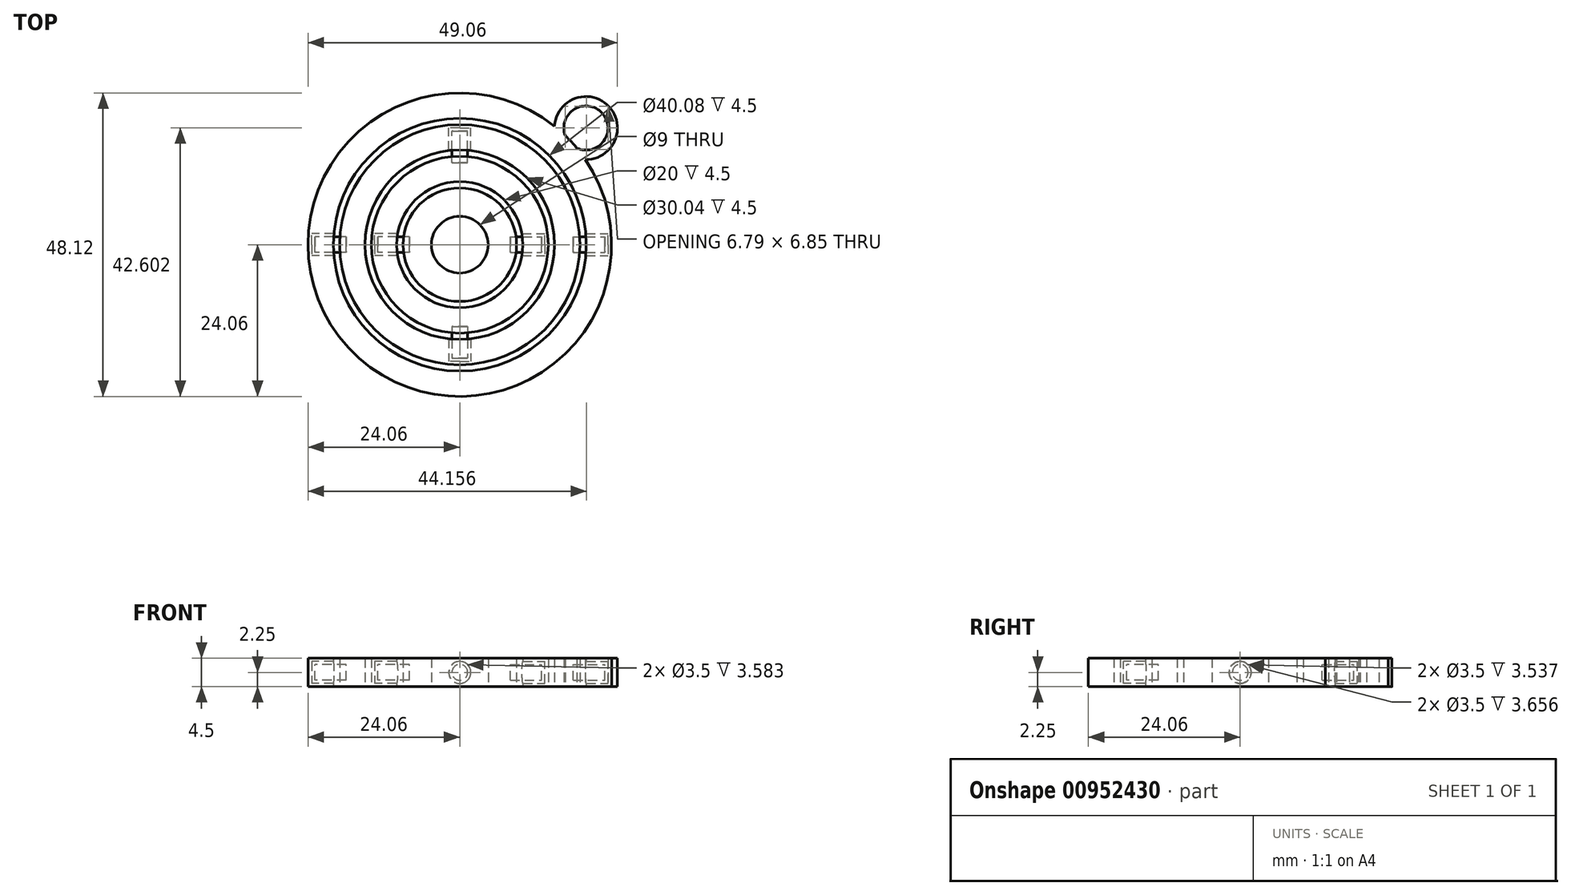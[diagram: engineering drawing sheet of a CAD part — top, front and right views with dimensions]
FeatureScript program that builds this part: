
annotation { "Feature Type Name" : "Feature", "Feature Type Description" : "" }
export const myFeature = defineFeature(function(context is Context, id is Id, definition is map)
    precondition{}
    {
        {
            var Q0;
            Q0=qCreatedBy(makeId("Top.planeOp"),FACE);
            var sketch = newSketch(context, id + "F0", { "sketchPlane" : qUnion([Q0])});
            skCircle(sketch, "E0", {"center": v(0, 0) * mm, "radius": 4.5 * mm});
            skCircle(sketch, "E1.0", {"center": v(0, 0) * mm, "radius": 9 * mm});
            skCircle(sketch, "E2.0", {"center": v(0, 0) * mm, "radius": 10 * mm});
            skCircle(sketch, "E3.0", {"center": v(0, 0) * mm, "radius": 14.02 * mm});
            skCircle(sketch, "E4.0", {"center": v(0, 0) * mm, "radius": 15.02 * mm});
            skCircle(sketch, "E5.0", {"center": v(0, 0) * mm, "radius": 19.04 * mm});
            skCircle(sketch, "E6.0", {"center": v(0, 0) * mm, "radius": 20.04 * mm});
            skCircle(sketch, "E7.0", {"center": v(0, 0) * mm, "radius": 24.06 * mm});
            skSolve(sketch);
        }
        {
            var Q0;
            Q0=qCreatedBy(makeId("Right.planeOp"),FACE);
            cPlane(context, id + "F1", {"entities" : qUnion([Q0]), "cplaneType" : CPlaneType.OFFSET, "offset" : 13 * mm, "oppositeDirection" : true, "width" : 150 * mm, "height" : 150 * mm});
        }
        {
            var Q0;
            Q0=qCreatedBy(makeId("Right.planeOp"),FACE);
            cPlane(context, id + "F2", {"entities" : qUnion([Q0]), "cplaneType" : CPlaneType.OFFSET, "offset" : 23 * mm, "oppositeDirection" : true, "width" : 150 * mm, "height" : 150 * mm});
        }
        {
            var Q0;
            Q0=makeQuery(id+"F0.imprint","IMPRINT",FACE,{"disambiguationData":[TD([[makeQuery(id+"F0.imprint","IMPRINT",EDGE,{"derivedFrom":sQuery(id+"F0.wireOp",EDGE,"E6.0")}),-1.0]])]});
            var Q1;
            Q1=makeQuery(id+"F0.imprint","IMPRINT",FACE,{"disambiguationData":[TD([[makeQuery(id+"F0.imprint","IMPRINT",EDGE,{"derivedFrom":sQuery(id+"F0.wireOp",EDGE,"E4.0")}),-1.0]])]});
            var Q2;
            Q2=makeQuery(id+"F0.imprint","IMPRINT",FACE,{"disambiguationData":[TD([[makeQuery(id+"F0.imprint","IMPRINT",EDGE,{"derivedFrom":sQuery(id+"F0.wireOp",EDGE,"E2.0")}),-1.0]])]});
            var Q3;
            Q3=makeQuery(id+"F0.imprint","IMPRINT",FACE,{"disambiguationData":[TD([[makeQuery(id+"F0.imprint","IMPRINT",EDGE,{"derivedFrom":sQuery(id+"F0.wireOp",EDGE,"E0")}),-1.0]])]});
            extrude(context, id + "F3", {"entities" : qUnion([Q0, Q1, Q2, Q3]), "depth" : 4.5 * mm, "offsetDistance" : 25 * mm});
        }
        {
            var Q0;
            Q0=qCreatedBy(id+"F1.planeOp",FACE);
            var sketch = newSketch(context, id + "F4", { "sketchPlane" : qUnion([Q0])});
            skCircle(sketch, "E8", {"center": v(0, 2.25) * mm, "radius": 1.25 * mm});
            skSolve(sketch);
        }
        {
            var Q0;
            Q0=makeQuery(id+"F4.imprint","IMPRINT",FACE,{"disambiguationData":[TD([[makeQuery(id+"F4.imprint","IMPRINT",EDGE,{"derivedFrom":sQuery(id+"F4.wireOp",EDGE,"E8")}),1.0]])]});
            extrude(context, id + "F5", {"entities" : qUnion([Q0]), "depth" : 5 * mm, "offsetDistance" : 25 * mm});
        }
        {
            var Q0;
            Q0=qCreatedBy(id+"F2.planeOp",FACE);
            var sketch = newSketch(context, id + "F6", { "sketchPlane" : qUnion([Q0])});
            skCircle(sketch, "E9.0", {"center": v(0, 2.25) * mm, "radius": 1.25 * mm});
            skSolve(sketch);
        }
        {
            var Q0;
            Q0=makeQuery(id+"F6.imprint","IMPRINT",FACE,{"disambiguationData":[TD([[makeQuery(id+"F6.imprint","IMPRINT",EDGE,{"derivedFrom":sQuery(id+"F6.wireOp",EDGE,"E9.0")}),1.0]])]});
            extrude(context, id + "F7", {"entities" : qUnion([Q0]), "depth" : 5 * mm, "offsetDistance" : 25 * mm});
        }
        {
            var Q0;
            Q0=qCreatedBy(id+"F1.planeOp",FACE);
            cPlane(context, id + "F8", {"entities" : qUnion([Q0]), "cplaneType" : CPlaneType.OFFSET, "offset" : 0.5 * mm, "oppositeDirection" : true, "width" : 150 * mm, "height" : 150 * mm});
        }
        {
            var Q0;
            Q0=qCreatedBy(id+"F2.planeOp",FACE);
            cPlane(context, id + "F9", {"entities" : qUnion([Q0]), "cplaneType" : CPlaneType.OFFSET, "offset" : 0.5 * mm, "oppositeDirection" : true, "width" : 150 * mm, "height" : 150 * mm});
        }
        {
            var Q0;
            Q0=qCreatedBy(id+"F8.planeOp",FACE);
            var sketch = newSketch(context, id + "F10", { "sketchPlane" : qUnion([Q0])});
            skCircle(sketch, "E10.0", {"center": v(0, 2.25) * mm, "radius": 1.25 * mm});
            skCircle(sketch, "E11.0", {"center": v(0, 2.25) * mm, "radius": 1.75 * mm});
            skSolve(sketch);
        }
        {
            var Q0;
            Q0=qCreatedBy(id+"F9.planeOp",FACE);
            var sketch = newSketch(context, id + "F11", { "sketchPlane" : qUnion([Q0])});
            skCircle(sketch, "E12.0", {"center": v(0, 2.25) * mm, "radius": 1.25 * mm});
            skCircle(sketch, "E13.0", {"center": v(0, 2.25) * mm, "radius": 1.75 * mm});
            skSolve(sketch);
        }
        {
            var Q0;
            Q0=makeQuery(id+"F10.imprint","IMPRINT",FACE,{"disambiguationData":[TD([[makeQuery(id+"F10.imprint","IMPRINT",EDGE,{"derivedFrom":sQuery(id+"F10.wireOp",EDGE,"E10.0")}),-1.0]])]});
            var Q1;
            Q1=makeQuery(id+"F10.imprint","IMPRINT",FACE,{"disambiguationData":[TD([[makeQuery(id+"F10.imprint","IMPRINT",EDGE,{"derivedFrom":sQuery(id+"F10.wireOp",EDGE,"E10.0")}),1.0]])]});
            extrude(context, id + "F12", {"entities" : qUnion([Q0, Q1]), "depth" : 5 * mm, "offsetDistance" : 25 * mm});
        }
        {
            var Q0;
            Q0=makeQuery(id+"F11.imprint","IMPRINT",FACE,{"disambiguationData":[TD([[makeQuery(id+"F11.imprint","IMPRINT",EDGE,{"derivedFrom":sQuery(id+"F11.wireOp",EDGE,"E12.0")}),1.0]])]});
            var Q1;
            Q1=makeQuery(id+"F11.imprint","IMPRINT",FACE,{"disambiguationData":[TD([[makeQuery(id+"F11.imprint","IMPRINT",EDGE,{"derivedFrom":sQuery(id+"F11.wireOp",EDGE,"E12.0")}),-1.0]])]});
            extrude(context, id + "F13", {"entities" : qUnion([Q0, Q1]), "depth" : 5 * mm, "offsetDistance" : 25 * mm});
        }
        {
            var Q0;
            Q0=makeQuery(id+"F5.opExtrude","SWEPT_BODY",BODY,{"disambiguationData":[OSD([sQuery(id+"F4.wireOp",EDGE,"E8")])]});
            var Q1;
            Q1=makeQuery(id+"F7.opExtrude","SWEPT_BODY",BODY,{"disambiguationData":[OSD([sQuery(id+"F6.wireOp",EDGE,"E9.0")])]});
            var Q2;
            Q2=makeQuery(id+"F12.opExtrude","SWEPT_BODY",BODY,{"disambiguationData":[OSD([sQuery(id+"F10.wireOp",EDGE,"E11.0")])]});
            var Q3;
            Q3=makeQuery(id+"F13.opExtrude","SWEPT_BODY",BODY,{"disambiguationData":[OSD([sQuery(id+"F11.wireOp",EDGE,"E13.0")])]});
            var Q4;
            Q4=qCreatedBy(makeId("Right.planeOp"),FACE);
            mirror(context, id + "F14", {"entities" : qUnion([Q0, Q1, Q2, Q3]), "mirrorPlane" : qUnion([Q4])});
        }
        {
            var Q0;
            Q0=qCreatedBy(makeId("Front.planeOp"),FACE);
            cPlane(context, id + "F15", {"entities" : qUnion([Q0]), "cplaneType" : CPlaneType.OFFSET, "offset" : 18 * mm, "oppositeDirection" : true, "width" : 150 * mm, "height" : 150 * mm});
        }
        {
            var Q0;
            Q0=qCreatedBy(id+"F15.planeOp",FACE);
            var sketch = newSketch(context, id + "F16", { "sketchPlane" : qUnion([Q0])});
            skCircle(sketch, "E14", {"center": v(0, 2.25) * mm, "radius": 1.25 * mm});
            skSolve(sketch);
        }
        {
            var Q0;
            Q0=makeQuery(id+"F16.imprint","IMPRINT",FACE,{"disambiguationData":[TD([[makeQuery(id+"F16.imprint","IMPRINT",EDGE,{"derivedFrom":sQuery(id+"F16.wireOp",EDGE,"E14")}),1.0]])]});
            extrude(context, id + "F17", {"entities" : qUnion([Q0]), "depth" : 5 * mm, "offsetDistance" : 25 * mm});
        }
        {
            var Q0;
            Q0=qCreatedBy(id+"F15.planeOp",FACE);
            cPlane(context, id + "F18", {"entities" : qUnion([Q0]), "cplaneType" : CPlaneType.OFFSET, "offset" : 0.5 * mm, "oppositeDirection" : true, "width" : 150 * mm, "height" : 150 * mm});
        }
        {
            var Q0;
            Q0=qCreatedBy(id+"F18.planeOp",FACE);
            var sketch = newSketch(context, id + "F19", { "sketchPlane" : qUnion([Q0])});
            skCircle(sketch, "E15.0", {"center": v(0, 2.25) * mm, "radius": 1.25 * mm});
            skCircle(sketch, "E16.0", {"center": v(0, 2.25) * mm, "radius": 1.75 * mm});
            skSolve(sketch);
        }
        {
            var Q0;
            Q0=makeQuery(id+"F19.imprint","IMPRINT",FACE,{"disambiguationData":[TD([[makeQuery(id+"F19.imprint","IMPRINT",EDGE,{"derivedFrom":sQuery(id+"F19.wireOp",EDGE,"E15.0")}),1.0]])]});
            var Q1;
            Q1=makeQuery(id+"F19.imprint","IMPRINT",FACE,{"disambiguationData":[TD([[makeQuery(id+"F19.imprint","IMPRINT",EDGE,{"derivedFrom":sQuery(id+"F19.wireOp",EDGE,"E15.0")}),-1.0]])]});
            extrude(context, id + "F20", {"entities" : qUnion([Q0, Q1]), "depth" : 5 * mm, "offsetDistance" : 25 * mm});
        }
        {
            var Q0;
            Q0=makeQuery(id+"F17.opExtrude","SWEPT_BODY",BODY,{"disambiguationData":[OSD([sQuery(id+"F16.wireOp",EDGE,"E14")])]});
            var Q1;
            Q1=makeQuery(id+"F20.opExtrude","SWEPT_BODY",BODY,{"disambiguationData":[OSD([sQuery(id+"F19.wireOp",EDGE,"E16.0")])]});
            var Q2;
            Q2=qCreatedBy(makeId("Front.planeOp"),FACE);
            mirror(context, id + "F21", {"entities" : qUnion([Q0, Q1]), "mirrorPlane" : qUnion([Q2])});
        }
        {
            var Q0;
            Q0=makeQuery(id+"F13.opExtrude","SWEPT_BODY",BODY,{"disambiguationData":[OSD([sQuery(id+"F11.wireOp",EDGE,"E13.0")])]});
            var Q1;
            Q1=makeQuery(id+"F14.opPattern","COPY",BODY,{"derivedFrom":makeQuery(id+"F13.opExtrude","SWEPT_BODY",BODY,{"disambiguationData":[OSD([sQuery(id+"F11.wireOp",EDGE,"E13.0")])]}),"instanceName":"1"});
            var Q2;
            Q2=makeQuery(id+"F3.opExtrude","SWEPT_BODY",BODY,{"disambiguationData":[OSD([sQuery(id+"F0.wireOp",EDGE,"E6.0"),sQuery(id+"F0.wireOp",EDGE,"E7.0")])]});
            booleanBodies(context, id + "F22", {"operationType" : BooleanOperationType.SUBTRACTION, "tools" : qUnion([Q0, Q1]), "targets" : qUnion([Q2])});
        }
        {
            var Q0;
            Q0=makeQuery(id+"F12.opExtrude","SWEPT_BODY",BODY,{"disambiguationData":[OSD([sQuery(id+"F10.wireOp",EDGE,"E11.0")])]});
            var Q1;
            Q1=makeQuery(id+"F14.opPattern","COPY",BODY,{"derivedFrom":makeQuery(id+"F12.opExtrude","SWEPT_BODY",BODY,{"disambiguationData":[OSD([sQuery(id+"F10.wireOp",EDGE,"E11.0")])]}),"instanceName":"1"});
            var Q2;
            Q2=makeQuery(id+"F3.opExtrude","SWEPT_BODY",BODY,{"disambiguationData":[OSD([sQuery(id+"F0.wireOp",EDGE,"E2.0"),sQuery(id+"F0.wireOp",EDGE,"E3.0")])]});
            booleanBodies(context, id + "F23", {"operationType" : BooleanOperationType.SUBTRACTION, "tools" : qUnion([Q0, Q1]), "targets" : qUnion([Q2])});
        }
        {
            var Q0;
            Q0=makeQuery(id+"F20.opExtrude","SWEPT_BODY",BODY,{"disambiguationData":[OSD([sQuery(id+"F19.wireOp",EDGE,"E16.0")])]});
            var Q1;
            Q1=makeQuery(id+"F21.opPattern","COPY",BODY,{"derivedFrom":makeQuery(id+"F20.opExtrude","SWEPT_BODY",BODY,{"disambiguationData":[OSD([sQuery(id+"F19.wireOp",EDGE,"E16.0")])]}),"instanceName":"1"});
            var Q2;
            Q2=makeQuery(id+"F3.opExtrude","SWEPT_BODY",BODY,{"disambiguationData":[OSD([sQuery(id+"F0.wireOp",EDGE,"E4.0"),sQuery(id+"F0.wireOp",EDGE,"E5.0")])]});
            booleanBodies(context, id + "F24", {"operationType" : BooleanOperationType.SUBTRACTION, "tools" : qUnion([Q0, Q1]), "targets" : qUnion([Q2])});
        }
        {
            var Q0;
            Q0=qCreatedBy(makeId("Top.planeOp"),FACE);
            var sketch = newSketch(context, id + "F25", { "sketchPlane" : qUnion([Q0])});
            skCircle(sketch, "E17", {"center": v(20, 18.5) * mm, "radius": 5 * mm});
            skCircle(sketch, "E18.0", {"center": v(20, 18.5) * mm, "radius": 3.5 * mm});
            skSolve(sketch);
        }
        {
            var Q0;
            Q0=makeQuery(id+"F25.imprint","IMPRINT",FACE,{"disambiguationData":[TD([[makeQuery(id+"F25.imprint","IMPRINT",EDGE,{"derivedFrom":sQuery(id+"F25.wireOp",EDGE,"E17")}),1.0]])]});
            extrude(context, id + "F26", {"entities" : qUnion([Q0]), "operationType" : NewBodyOperationType.ADD, "depth" : 4.5 * mm, "offsetDistance" : 25 * mm});
        }
    });
